# Revit family: FP_Revit_18_OR30SCG6W1_Range_90000999A
name_source: partatom
category: Specialty Equipment
revit_build: Autodesk Revit 2018 (Build: 20170223_1515(x64)
units: mm (PartAtom-declared; Revit-internal decimal feet)

## family parameters
Always vertical = Yes
Cut with Voids When Loaded = Yes
OmniClass Number = 23.40.40.14.17.17
OmniClass Title = Ranges
Part Type = Normal
Room Calculation Point = No
Round Connector Dimension = Use Diameter
Shared = No
Work Plane-Based = No

## types (4) — shared parameters
Cavity - Depth = 641 mm  [stored 2.10302 ft]
Cavity - Width = 762 mm  [stored 2.5 ft]
Chassis - Depth = 638 mm  [stored 2.09318 ft]
Chassis - Height = 816 mm
Chassis - Width = 759 mm  [stored 2.49016 ft]
Clearance - Overhead Combustible = 914 mm
Clearance - Overhead Non-Combustible = 762 mm  [stored 2.5 ft]
Clearance - Overhead Rangehood = 762 mm  [stored 2.5 ft]
Clearance - Rear Combustible = 305 mm
Clearance - Side Combustible = 330 mm  [stored 1.08268 ft]
Connector Description - Electrical = 120/208 V or 120/240 V, 60Hz, 30 A, Fused electrical supply
Connector Description - Gas = NG 1kPa (4" WC), LPG 2.75 kPa (11" WC), 1/2” NPT Minimum 5/8” dia. flex line
Countertop Height (min 908mm - max 933mm) = 915 mm  [stored 3.00197 ft]
Manufacturer = Fisher & Paykel Appliances
Material - Body = Fisher & Paykel - Stainless Steel
Material - Burners & Trivets = Fisher & Paykel - Black, Matte
Material - Buttons and Dials = Fisher & Paykel - Steel, Chrome Plated
Material - Door Front = Fisher & Paykel - Glass, Black
Material - Handle = Fisher & Paykel - Stainless Steel
Material - Trim = Fisher & Paykel - Steel, Chrome Plated
Optional - Rear Trim = TKOR306X1
Product - Depth = 693 mm
Product - Height = 915 mm  [stored 3.00197 ft]
Product - Width = 759 mm  [stored 2.49016 ft]
URL = www.fisherpaykel.com
Visibility - Adjustable Feet Covers = Yes
Visibility - Clearance Required = Yes
Visibility - Rear Trim (Supplied) = Yes
Visibility - Rear Trim 3"/76mm (Optional) = No
Visibility - Toe Kick Panel (Optional) = Yes
zero-valued in all types: Cavity - Height, Clearance - Rear Non-Combustible, Clearance - Side Non-Combustible

## per-type parameters (varying)
| type | Description | Material - COLOUR CHANGE | Model | Optional - Toe Kick Panel |
| OR30SCG6B (Black) | 30" Classic Freestanding Dual Fuel Range (Stainless) | Fisher & Paykel - Black | OR30SCG6B1 | KICKOR30B1 |
| OR30SCG6W (White) | 30" Classic Freestanding Dual Fuel Range (White) | Fisher & Paykel - White | OR30SCG6W1 | KICKOR30W1 |
| OR30SCG6R (Red) | 30" Classic Freestanding Dual Fuel Range (Red) | Fisher & Paykel - Red | OR30SCG6R1 | KICKOR30R1 |
| OR30SCG6X (Stainless) | 30" Classic Freestanding Dual Fuel Range (Stainless) | Fisher & Paykel - Stainless Steel | OR30SCG6X1 | KICKOR30X1 |

note: [stored X ft] marks values corroborated as IEEE doubles in the binary element streams (Revit-internal decimal feet)

## geometry (parser evidence)
native form markers: Sweep x19
no freeform markers — native parametric forms only
